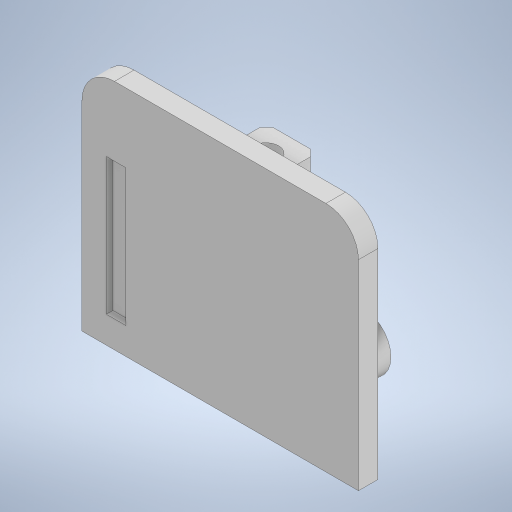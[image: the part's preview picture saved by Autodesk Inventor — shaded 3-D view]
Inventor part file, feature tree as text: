
AUTODESK INVENTOR PART (.ipt)
format: ipt  version: 2023 (Build 270158000, 158)  size: 324,096 bytes
history: native  units: mm
features: extrude x7, sketch x7, other x2, pattern_linear x2, chamfer x2, projected_geometry x2, fillet x1
ambient origin geometry x8: Origin, YZ Plane, XZ Plane, XY Plane, X Axis, Y Axis, Z Axis, Center Point
bodies: Body1 (feature_tree)
feature tree (23):
  other  "솔리드1"
  extrude  "돌출1"  Depth=42.5mm
  fillet  "모깎기1"  Radius=36.25mm
  other  "작업 평면1"
  extrude  "돌출2"  Depth=3.0mm TaperAngle=0.0deg
  pattern_linear  "직사각형 패턴1"  Spacing1=5.0mm  [1 undecoded]
  extrude  "돌출3"  [1 undecoded]
  extrude  "돌출4"  Depth=4.0mm
  extrude  "돌출5"  Depth=4.0mm
  chamfer  "모따기1"  Distance=8.0mm
  extrude  "돌출6"  Depth=10.0mm
  extrude  "돌출7"  Depth=2.0mm TaperAngle=0.0deg
  pattern_linear  "직사각형 패턴2"  Count1=2 Spacing1=22.5mm
  chamfer  "모따기2"  Distance=15.8mm
  sketch  "스케치1"
  sketch  "스케치2"
  sketch  "스케치3"
  sketch  "스케치4"
  sketch  "스케치5"
  sketch  "스케치6"
  projected_geometry  "투영된 루프1"
  projected_geometry  "투영된 루프2"
  sketch  "스케치7"
note: 2 required parameter values undecoded (feature->parameter linkage not recoverable at this tier; creation-order binding heuristic only, values carry confidence <= 0.55)
